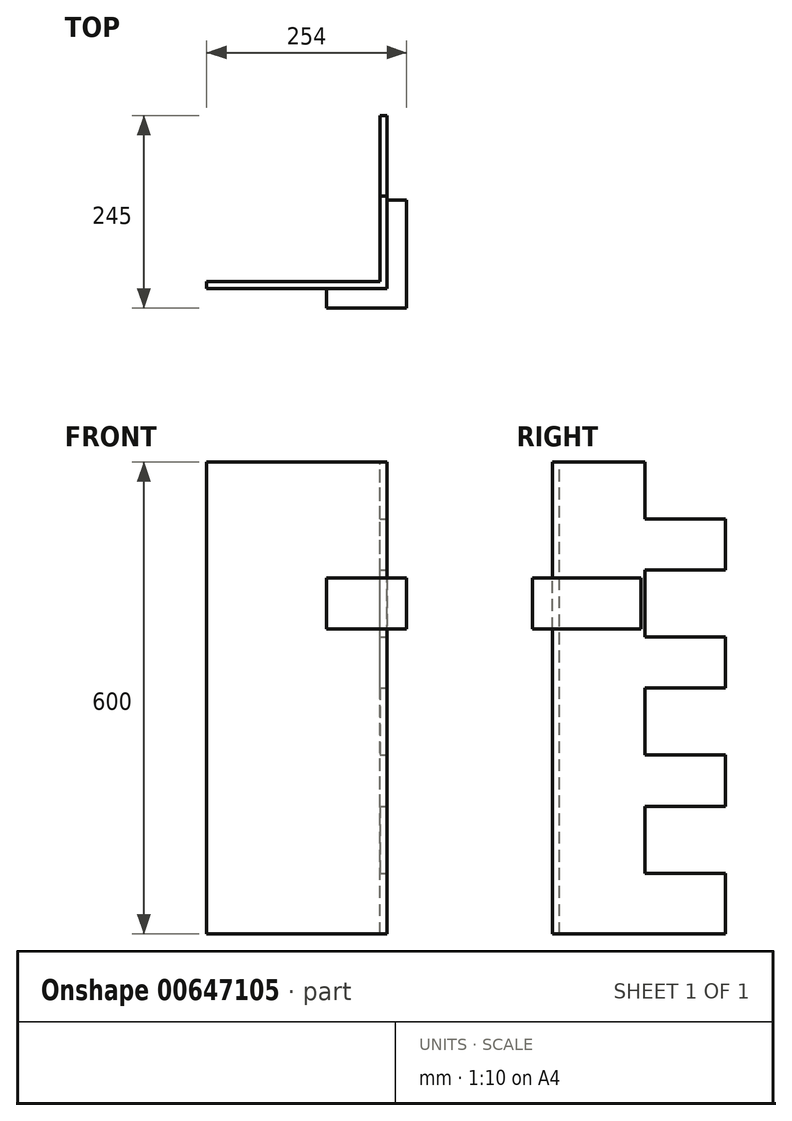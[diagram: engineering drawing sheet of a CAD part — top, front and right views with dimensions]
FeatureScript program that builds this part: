
annotation { "Feature Type Name" : "Feature", "Feature Type Description" : "" }
export const myFeature = defineFeature(function(context is Context, id is Id, definition is map)
    precondition{}
    {
        {
            var Q0;
            Q0=qCreatedBy(makeId("Front.planeOp"),FACE);
            var sketch = newSketch(context, id + "F0", { "sketchPlane" : qUnion([Q0])});
            skLineSegment(sketch, "E0.bottom", {"start": v(0, 0) * mm, "end": v(-220, 0) * mm});
            skLineSegment(sketch, "E0.top", {"start": v(0, 600) * mm, "end": v(-220, 600) * mm});
            skLineSegment(sketch, "E0.left", {"start": v(0, 0) * mm, "end": v(0, 600) * mm});
            skLineSegment(sketch, "E0.right", {"start": v(-220, 0) * mm, "end": v(-220, 600) * mm});
            skSolve(sketch);
        }
        {
            var Q0;
            Q0=qSketchRegion(id+"F0",true);
            extrude(context, id + "F1", {"entities" : qUnion([Q0]), "depth" : 9 * mm, "offsetDistance" : 25 * mm});
        }
        {
            var Q0;
            Q0=qCreatedBy(makeId("Right.planeOp"),FACE);
            var sketch = newSketch(context, id + "F2", { "sketchPlane" : qUnion([Q0])});
            skLineSegment(sketch, "E1", {"start": v(0, 0) * mm, "end": v(-9, 0) * mm});
            skLineSegment(sketch, "E2.bottom", {"start": v(-9, 0) * mm, "end": v(211, 0) * mm});
            skLineSegment(sketch, "E2.top", {"start": v(-9, 600) * mm, "end": v(211, 600) * mm});
            skLineSegment(sketch, "E2.left", {"start": v(-9, 0) * mm, "end": v(-9, 600) * mm});
            skLineSegment(sketch, "E2.right", {"start": v(211, 0) * mm, "end": v(211, 600) * mm});
            skSolve(sketch);
        }
        {
            var Q0;
            Q0=qSketchRegion(id+"F2",true);
            extrude(context, id + "F3", {"entities" : qUnion([Q0]), "depth" : 9 * mm, "offsetDistance" : 25 * mm});
        }
        {
            var Q0;
            Q0=makeQuery(id+"F3.opExtrude","CAP_FACE",FACE,{"disambiguationData":[OSD([sQuery(id+"F2.wireOp",EDGE,"E2.bottom"),sQuery(id+"F2.wireOp",EDGE,"E2.top"),sQuery(id+"F2.wireOp",EDGE,"E2.left"),sQuery(id+"F2.wireOp",EDGE,"E2.right")])],"isStart":false});
            var sketch = newSketch(context, id + "F4", { "sketchPlane" : qUnion([Q0])});
            skLineSegment(sketch, "E3", {"start": v(108.5, 312.42) * mm, "end": v(211, 312.42) * mm});
            skLineSegment(sketch, "E4", {"start": v(211, 377.42) * mm, "end": v(108.5, 377.42) * mm});
            skLineSegment(sketch, "E5", {"start": v(108.5, 377.42) * mm, "end": v(108.5, 462.42) * mm});
            skLineSegment(sketch, "E6", {"start": v(108.5, 462.42) * mm, "end": v(211, 462.42) * mm});
            skLineSegment(sketch, "E7", {"start": v(211, 527.42) * mm, "end": v(108.5, 527.42) * mm});
            skLineSegment(sketch, "E8", {"start": v(108.5, 527.42) * mm, "end": v(108.5, 600) * mm});
            skLineSegment(sketch, "E9", {"start": v(108.5, 312.42) * mm, "end": v(108.5, 227.42) * mm});
            skLineSegment(sketch, "E10", {"start": v(108.5, 227.42) * mm, "end": v(211, 227.42) * mm});
            skLineSegment(sketch, "E11", {"start": v(211, 162.42) * mm, "end": v(108.5, 162.42) * mm});
            skLineSegment(sketch, "E12", {"start": v(108.5, 162.42) * mm, "end": v(108.5, 77.42) * mm});
            skLineSegment(sketch, "E13", {"start": v(108.5, 77.42) * mm, "end": v(211, 77.42) * mm});
            skLineSegment(sketch, "E14", {"start": v(211, 77.42) * mm, "end": v(211, 600) * mm});
            skLineSegment(sketch, "E15", {"start": v(211, 600) * mm, "end": v(108.5, 600) * mm});
            skSolve(sketch);
        }
        {
            var Q0;
            Q0=qSketchRegion(id+"F4",true);
            extrude(context, id + "F5", {"entities" : qUnion([Q0]), "operationType" : NewBodyOperationType.REMOVE, "oppositeDirection" : true, "depth" : 25 * mm, "offsetDistance" : 25 * mm});
        }
        {
            var Q0;
            Q0=makeQuery(id+"F3.opExtrude","CAP_FACE",FACE,{"disambiguationData":[OSD([sQuery(id+"F2.wireOp",EDGE,"E2.bottom"),sQuery(id+"F2.wireOp",EDGE,"E2.top"),sQuery(id+"F2.wireOp",EDGE,"E2.left"),sQuery(id+"F2.wireOp",EDGE,"E2.right")])],"isStart":false});
            var sketch = newSketch(context, id + "F6", { "sketchPlane" : qUnion([Q0])});
            skLineSegment(sketch, "E16", {"start": v(103.5, 387.42) * mm, "end": v(-9, 387.42) * mm});
            skLineSegment(sketch, "E17", {"start": v(-9, 387.42) * mm, "end": v(-34, 387.42) * mm});
            skLineSegment(sketch, "E18", {"start": v(-34, 387.42) * mm, "end": v(-34, 452.42) * mm});
            skLineSegment(sketch, "E19", {"start": v(-34, 452.42) * mm, "end": v(103.5, 452.42) * mm});
            skLineSegment(sketch, "E20", {"start": v(103.5, 452.42) * mm, "end": v(103.5, 387.42) * mm});
            skSolve(sketch);
        }
        {
            var Q0;
            {var subQ0=sQuery(id+"F6.wireOp",EDGE,"E16");Q0=makeQuery(id+"F6.imprint","IMPRINT",FACE,{"disambiguationData":[TD([[makeQuery(id+"F6.imprint","IMPRINT",EDGE,{"derivedFrom":subQ0}),-1.0]])]});}
            var Q1;
            {var subQ0=sQuery(id+"F6.wireOp",EDGE,"E17");Q1=makeQuery(id+"F6.imprint","IMPRINT",FACE,{"disambiguationData":[TD([[makeQuery(id+"F6.imprint","IMPRINT",EDGE,{"derivedFrom":subQ0}),-1.0]])]});}
            extrude(context, id + "F7", {"entities" : qUnion([Q0, Q1]), "operationType" : NewBodyOperationType.ADD, "depth" : 25 * mm, "offsetDistance" : 25 * mm});
        }
        {
            var Q0;
            Q0=makeQuery(id+"F7.opExtrude","CAP_FACE",FACE,{"disambiguationData":[OSD([sQuery(id+"F6.wireOp",EDGE,"E16"),sQuery(id+"F6.wireOp",EDGE,"E17"),sQuery(id+"F6.wireOp",EDGE,"E18"),sQuery(id+"F6.wireOp",EDGE,"E19"),sQuery(id+"F6.wireOp",EDGE,"E20")])],"isStart":true});
            var sketch = newSketch(context, id + "F8", { "sketchPlane" : qUnion([Q0])});
            skLineSegment(sketch, "E21.bottom", {"start": v(34, 387.42) * mm, "end": v(9, 387.42) * mm});
            skLineSegment(sketch, "E21.top", {"start": v(34, 452.42) * mm, "end": v(9, 452.42) * mm});
            skLineSegment(sketch, "E21.left", {"start": v(34, 387.42) * mm, "end": v(34, 452.42) * mm});
            skLineSegment(sketch, "E21.right", {"start": v(9, 387.42) * mm, "end": v(9, 452.42) * mm});
            skSolve(sketch);
        }
        {
            var Q0;
            Q0=qSketchRegion(id+"F8",true);
            extrude(context, id + "F9", {"entities" : qUnion([Q0]), "operationType" : NewBodyOperationType.ADD, "depth" : (102 - 25) * mm, "offsetDistance" : 25 * mm});
        }
    });
